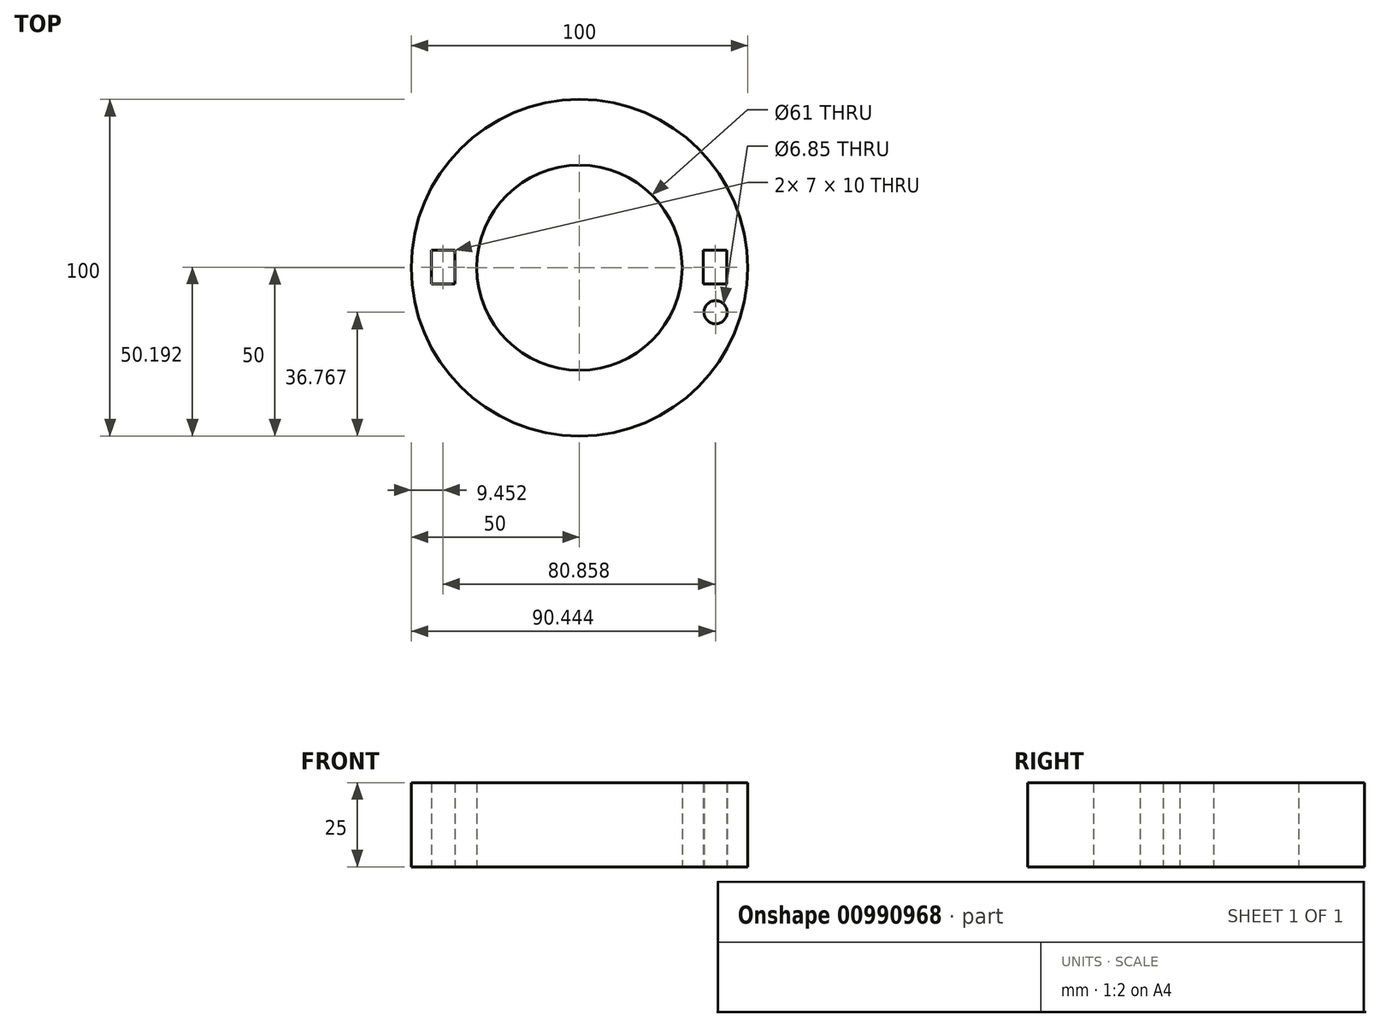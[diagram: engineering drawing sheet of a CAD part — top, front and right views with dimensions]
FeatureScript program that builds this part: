
annotation { "Feature Type Name" : "Feature", "Feature Type Description" : "" }
export const myFeature = defineFeature(function(context is Context, id is Id, definition is map)
    precondition{}
    {
        {
            var Q0;
            Q0=qCreatedBy(makeId("Top.planeOp"),FACE);
            var sketch = newSketch(context, id + "F0", { "sketchPlane" : qUnion([Q0])});
            skCircle(sketch, "E0", {"center": v(-40.68, -13.23) * mm, "radius": 3.43 * mm});
            skLineSegment(sketch, "E1", {"start": v(-0.12, 50.2) * mm, "end": v(-0.12, -49.8) * mm, "construction": true});
            skCircle(sketch, "E2.MirrorC", {"center": v(40.44, -13.23) * mm, "radius": 3.43 * mm});
            skLineSegment(sketch, "E3.bottom", {"start": v(-37.05, -4.8) * mm, "end": v(-44.05, -4.8) * mm});
            skLineSegment(sketch, "E3.top", {"start": v(-37.05, 5.2) * mm, "end": v(-44.05, 5.2) * mm});
            skLineSegment(sketch, "E3.left", {"start": v(-37.05, -4.8) * mm, "end": v(-37.05, 5.2) * mm});
            skLineSegment(sketch, "E3.right", {"start": v(-44.05, -4.8) * mm, "end": v(-44.05, 5.2) * mm});
            skLineSegment(sketch, "E4.MirrorCS", {"start": v(36.81, 5.2) * mm, "end": v(43.81, 5.2) * mm});
            skLineSegment(sketch, "E5.MirrorCS", {"start": v(36.81, -4.8) * mm, "end": v(36.81, 5.2) * mm});
            skLineSegment(sketch, "E6.MirrorCS", {"start": v(36.81, -4.8) * mm, "end": v(43.81, -4.8) * mm});
            skLineSegment(sketch, "E7.MirrorCS", {"start": v(43.81, -4.8) * mm, "end": v(43.81, 5.2) * mm});
            skCircle(sketch, "E8", {"center": v(0, 0) * mm, "radius": 30.5 * mm});
            skCircle(sketch, "E9", {"center": v(0, 0) * mm, "radius": 50 * mm});
            skSolve(sketch);
        }
        {
            var Q0;
            Q0=makeQuery(id+"F0.imprint","IMPRINT",FACE,{"disambiguationData":[TD([[makeQuery(id+"F0.imprint","IMPRINT",EDGE,{"derivedFrom":sQuery(id+"F0.wireOp",EDGE,"e0b62fb5-1751-473e-acd3-66306070ded0.bottom")}),1.0]])]});
            var Q1;
            Q1=makeQuery(id+"F0.imprint","IMPRINT",FACE,{"disambiguationData":[TD([[makeQuery(id+"F0.imprint","IMPRINT",EDGE,{"derivedFrom":sQuery(id+"F0.wireOp",EDGE,"E0")}),-1.0]])]});
            var Q2;
            Q2=makeQuery(id+"F0.imprint","IMPRINT",FACE,{"disambiguationData":[TD([[makeQuery(id+"F0.imprint","IMPRINT",EDGE,{"derivedFrom":sQuery(id+"F0.wireOp",EDGE,"E0")}),1.0]])]});
            var Q3;
            Q3=makeQuery(id+"F0.imprint","IMPRINT",FACE,{"disambiguationData":[TD([[makeQuery(id+"F0.imprint","IMPRINT",EDGE,{"derivedFrom":sQuery(id+"F0.wireOp",EDGE,"E2.MirrorC")}),-1.0]])]});
            extrude(context, id + "F1", {"entities" : qUnion([Q0, Q1, Q2, Q3]), "depth" : 10 * mm, "offsetDistance" : 25 * mm});
        }
        {
            var Q0;
            Q0=makeQuery(id+"F0.imprint","IMPRINT",FACE,{"disambiguationData":[TD([[makeQuery(id+"F0.imprint","IMPRINT",EDGE,{"derivedFrom":sQuery(id+"F0.wireOp",EDGE,"E0")}),1.0]])]});
            var Q1;
            Q1=makeQuery(id+"F0.imprint","IMPRINT",FACE,{"disambiguationData":[TD([[makeQuery(id+"F0.imprint","IMPRINT",EDGE,{"derivedFrom":sQuery(id+"F0.wireOp",EDGE,"E2.MirrorC")}),-1.0]])]});
            extrude(context, id + "F2", {"entities" : qUnion([Q0, Q1]), "operationType" : NewBodyOperationType.ADD, "depth" : 25 * mm, "offsetDistance" : 25 * mm});
        }
    });
